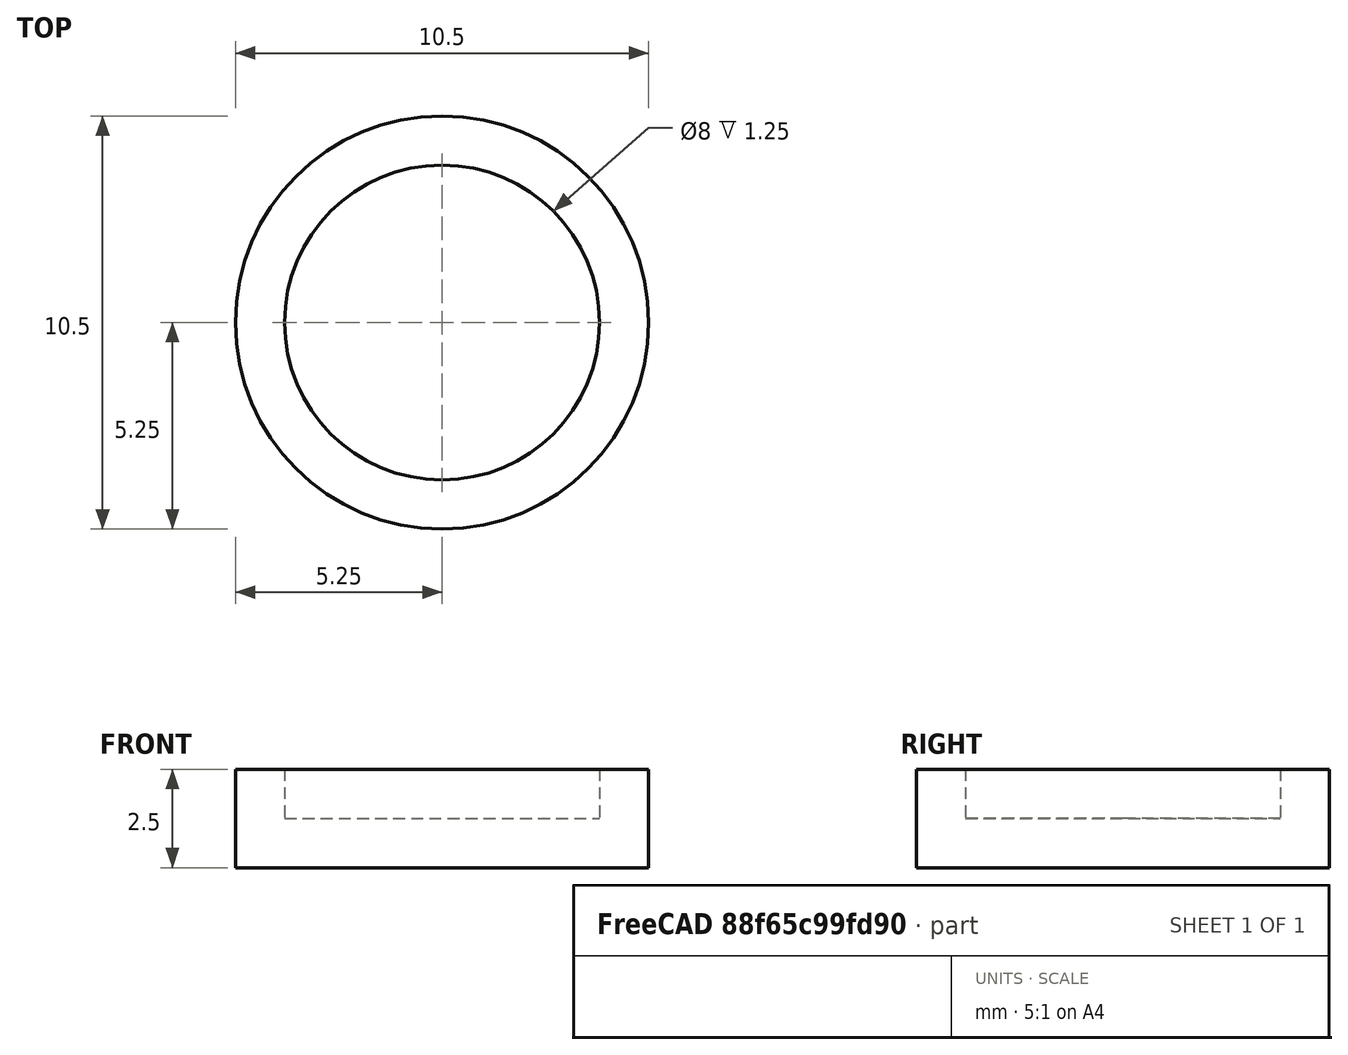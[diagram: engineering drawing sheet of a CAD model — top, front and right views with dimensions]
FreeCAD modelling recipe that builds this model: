
FCSTD DOCUMENT  (FreeCAD 0.21R33771 (Git))
Label: payload-carrier
License: All rights reserved
LicenseURL: http://en.wikipedia.org/wiki/All_rights_reserved
objects: Sketcher::SketchObject×1, PartDesign::Revolution×1, PartDesign::Body×1
note: 4 computed .brp shape members not serialized (recipe doc carries the construction recipe); baked Part::Feature solids carry a one-line shape summary decoded from their .brp

FEATURE [Sketcher::SketchObject] Sketch
  FullyConstrained = true
  MapMode = 5
  Placement = pos=(0,0,0) rot=(1,0,0;1.5708rad)
  Support = -> [XZ_Plane]
  sketch-geometry (6):
    g0: LineSegment StartX=0 StartY=0 StartZ=0 EndX=-5.25 EndY=0 EndZ=0
    g1: LineSegment StartX=-5.25 StartY=0 StartZ=0 EndX=-5.25 EndY=2.5 EndZ=0
    g2: LineSegment StartX=-5.25 StartY=2.5 StartZ=0 EndX=-4 EndY=2.5 EndZ=0
    g3: LineSegment StartX=-4 StartY=2.5 StartZ=0 EndX=-4 EndY=1.25 EndZ=0
    g4: LineSegment StartX=-4 StartY=1.25 StartZ=0 EndX=0 EndY=1.25 EndZ=0
    g5: LineSegment StartX=0 StartY=1.25 StartZ=0 EndX=0 EndY=0 EndZ=0
  constraints (17):
    c: Coincident(g0,g-1)
    c: PointOnObject(g0,g-1)
    c: Coincident(g1,g0)
    c: Vertical(g1)
    c: Coincident(g2,g1)
    c: Horizontal(g2)
    c: DistanceX(g0,g0) = 5.25
    c: DistanceY(g1,g1) = 2.5
    c: DistanceX(g2,g2) = 1.25
    c: Coincident(g3,g2)
    c: Vertical(g3)
    c: DistanceY(g3,g3) = 1.25
    c: Coincident(g4,g3)
    c: PointOnObject(g4,g-2)
    c: Horizontal(g4)
    c: Coincident(g5,g4)
    c: Coincident(g5,g0)
FEATURE [PartDesign::Revolution] Revolution
  Angle = 360
  Axis = (0,-2e-16,1)
  Base = (0,0,0)
  Placement = pos=(0,0,0) rot=(1,0,0;1.5708rad)
  Profile = -> Sketch
  ReferenceAxis = -> Sketch [V_Axis]
FEATURE [PartDesign::Body] Body
  Group = -> [Sketch,Revolution]
  Origin = -> Origin
  Tip = -> Revolution
